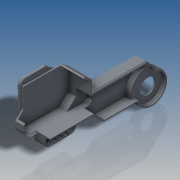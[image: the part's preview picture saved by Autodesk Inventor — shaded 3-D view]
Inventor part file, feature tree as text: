
AUTODESK INVENTOR PART (.ipt)
format: ipt  version: 2016 SP2 (Build 200236200, 236)  size: 832,512 bytes
history: native  units: in
note: dims shown in document units (in); Inventor stores cm internally (conversion verified against a paired STEP export)
features: extrude x17, sketch x7, plane x1, fillet x1
ambient origin geometry x8: Origin, YZ Plane, XZ Plane, XY Plane, X Axis, Y Axis, Z Axis, Center Point
bodies: Solid1 (feature_tree)
feature tree (26):
  sketch  "Sketch2"  dims[d0=0.9134in d1=0.8819in]
  extrude  "Extrusion1"  Depth=0.8819in
  extrude  "Extrusion2"  Depth=0.1417in
  extrude  "Extrusion3"  Depth=0.1417in
  sketch  "Sketch3"  dims[d2=0.4409in d4=0.1417in]
  extrude  "Extrusion7"  Depth=0.2992in
  extrude  "Extrusion4"  Depth=1.0866in
  extrude  "Extrusion5"  Depth=0.1575in
  extrude  "Extrusion6"  Depth=0.315in
  extrude  "Extrusion8"  Depth=0.0315in
  extrude  "Extrusion9"  Depth=0.0315in
  extrude  "Extrusion10"  Depth=0.0315in
  extrude  "Extrusion11"  Depth=0.1417in
  extrude  "Extrusion12"  Depth=0.0315in
  plane  "Work Plane2"
  sketch  "Sketch7"  dims[d9=1.4331in d10=1.0866in]
  extrude  "Extrusion16"  Depth=0.0315in
  extrude  "Extrusion17"  Depth=0.0315in
  extrude  "Extrusion18"  Depth=0.0315in
  extrude  "Extrusion20"  Depth=0.0315in
  extrude  "Extrusion21"  Depth=0.0315in
  fillet  "Fillet1"  Radius=0.0413in
  sketch  "Sketch4"  dims[d5=0.1417in d6=0.7717in]
  sketch  "Sketch5"  dims[d7=45.0deg d8=0.2992in]
  sketch  "Sketch9"  dims[d11=1.748in d12=0.1575in]
  sketch  "Sketch10"  dims[d13=0.2835in d14=0.315in d15=1.3543in d16=1.5591in d17=0.2992in d18=0.1417in d19=0.8119in d20=0.0472in d21=0.0557in d22=0.0472in d23=0.0945in d24=0.0472in d25=0.0413in d26=0.0472in d27=0.063in d28=0.0445in d29=0.0887in d32=0.0106in d33=0.2992in d34=0.0in d35=0.5039in d36=0.1417in d37=0.0in d38=0.2205in d39=0.0in d40=0.2835in d41=0.5669in d42=0.1102in d43=0.0157in d45=0.3937in d46=0.0in d47=0.1575in d48=0.0in d56=0.2047in d57=0.0787in d58=0.0in d60=0.1448in d61=0.0315in d62=-0.1855in d63=0.0315in d64=0.0in d75=1.9685in d77=0.0945in d78=0.3937in d80=0.3937in d82=0.0157in d83=0.0in d84=0.2677in d85=0.6457in d86=0.0in d87=0.2992in d88=0.315in d89=0.4094in d90=0.0in d91=0.252in d92=0.0in d93=0.0945in d94=0.0in d96=0.315in d101=0.0472in d111=-0.2992in d112=0.315in d114=0.0472in d115=0.2441in d116=0.189in d117=0.063in d118=0.063in d119=0.0in d120=0.252in d121=0.0in d122=0.315in d123=0.0in d127=0.0039in d128=0.0157in d129=0.1417in d130=0.1575in d131=0.315in d132=0.378in d133=0.5039in d134=1.2441in d135=0.1417in d136=1.0866in d137=0.1575in d138=0.1575in d139=0.2677in d140=0.6299in d141=0.0472in d142=1.9685in d144=0.0945in d145=0.3937in d147=0.3937in d149=0.3307in d150=0.1732in d151=0.2835in d152=45.0deg d153=0.252in d154=0.315in d155=0.0in d156=0.0157in d157=0.0157in d158=0.0157in d159=0.0157in d160=0.0157in d161=0.0157in d162=0.0157in d163=0.0157in d164=0.0157in d165=0.0315in d166=0.0in]
